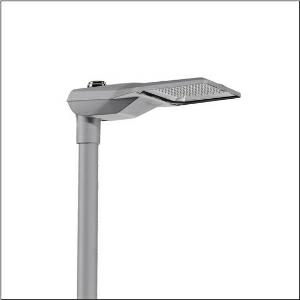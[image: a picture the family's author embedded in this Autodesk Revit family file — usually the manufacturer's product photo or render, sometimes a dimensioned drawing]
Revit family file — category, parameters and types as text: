
# Revit family: streetlight_sl_21_midi___st1_0a_5xe7d37n08lb_8a93
name_source: partatom
category: Lighting Fixtures
units: mm (PartAtom-declared; Revit-internal decimal feet)

## family parameters
Cut with Voids When Loaded = No
Host = Face
Light Source = No
Part Type = Normal
Room Calculation Point = No
Round Connector Dimension = Use Diameter
Shared = No

## types (1)
- --- (1 x LED, 14340 lm, 98.3 W, 3000K)
    Apparent Load = 98 VA
    CIE Flux Codes = 37 72 97 100 100
    Color Rendering = 70
    Color Temperature = 3000K
    Default Elevation = 1800 mm
    Description = Streetlight SL 21 midi, mast luminaire, primary light control with lens, of PMMA, primary optical cover: cover, of toughened safety glass, transparent, light distribution: ST1.0a, light emission: direct distribution, primary light characteristic: asymmetric, installation type: side-entry, LED, 3G 2.5mm², High Power LED, rated luminous flux: 14.340lm, luminous efficacy: 146lm/W, light colour: 730, colour temperature: 3000K, control gear: NEMA (7pin), control: overheat protection, pre-setting: linear dimming characteristic, constant luminous flux control, time-dependent luminous flux control, flexible luminous flux parameterisation, mains connection: 220..240V, AC, 50/60Hz, connection cable pre-assembled, cable length: 10,5m, wiring characteristics: H05VV-F, start of lifetime: 98W, end of service life: 101W, reduction: 45W, luminaire housing, of diecast aluminium (EN AC-44300), powder-coated, SITECO metallic grey (DB 702S), corrosivity category C5 high according to DIN EN ISO 12944, multi-level sealing system, sealing non-destructively replaceable, inclination adjustable: 0°, 5°, 10°, 15°, length: 644mm, width: 335mm, height: 110mm, spigot size: 42mm (side-entry), mounting height: 4..8m, protection rating (complete): IP66, insulation class (complete): insulation class I (protective earthing), certification: CE, ENEC, ENEC+, VDE, impact resistance: IK10, permissible operating ambient temperature for outdoor applications: -40..+50°C, standard-compliant lighting for roads and squares, packaging unit: 1 piece

Light Distribution: ST1.0a
    Height = 111 mm
    Lamp = 1 x LED
    Lamp Light Flux = 14340 lm
    Lamp Power = 98.3 W
    Lamp count = 1
    Length = 644 mm
    Luminous efficacy = 146 lm/W
    Manufacturer = Siteco
    ModVariant = No
    Model = 5XE7D37N08LB
    Number of Poles = 1
    OnlyDefault = Yes
    Power Factor = 1
    Product Name = Streetlight SL 21 midi | ST1.0a
    Product group = mast luminaire | pylon top
    ProductGroupID = 6100
    Protection Class = Protection class I
    Protection Degree = IP 66
    RLX_Detail_Level = 1
    RLX_Emergency_Light_Flux = 0 lm
    RLX_Emergency_Type = 0
    RLX_Emergency_Type_DB = No
    RlxData = <blob elided: 26661 chars, md5=97a787e2>
    Socket = socket
    Standby Power = 0 W
    System Light Flux = 14340 lm
    System Power = 98 W
    Type Comments = factory setting: luminous flux: 100 % | dim-lin: 254 | 1020 mA
    Type Image = l_1294377.jpg
    URL = http://relux.com
    VarID = @adj_135581
    Voltage = 0 V
    Weight = 0.00 kg
    Width = 336 mm

## geometry (parser evidence)
native form markers: Blend x4, Sweep x11
no freeform markers — native parametric forms only
